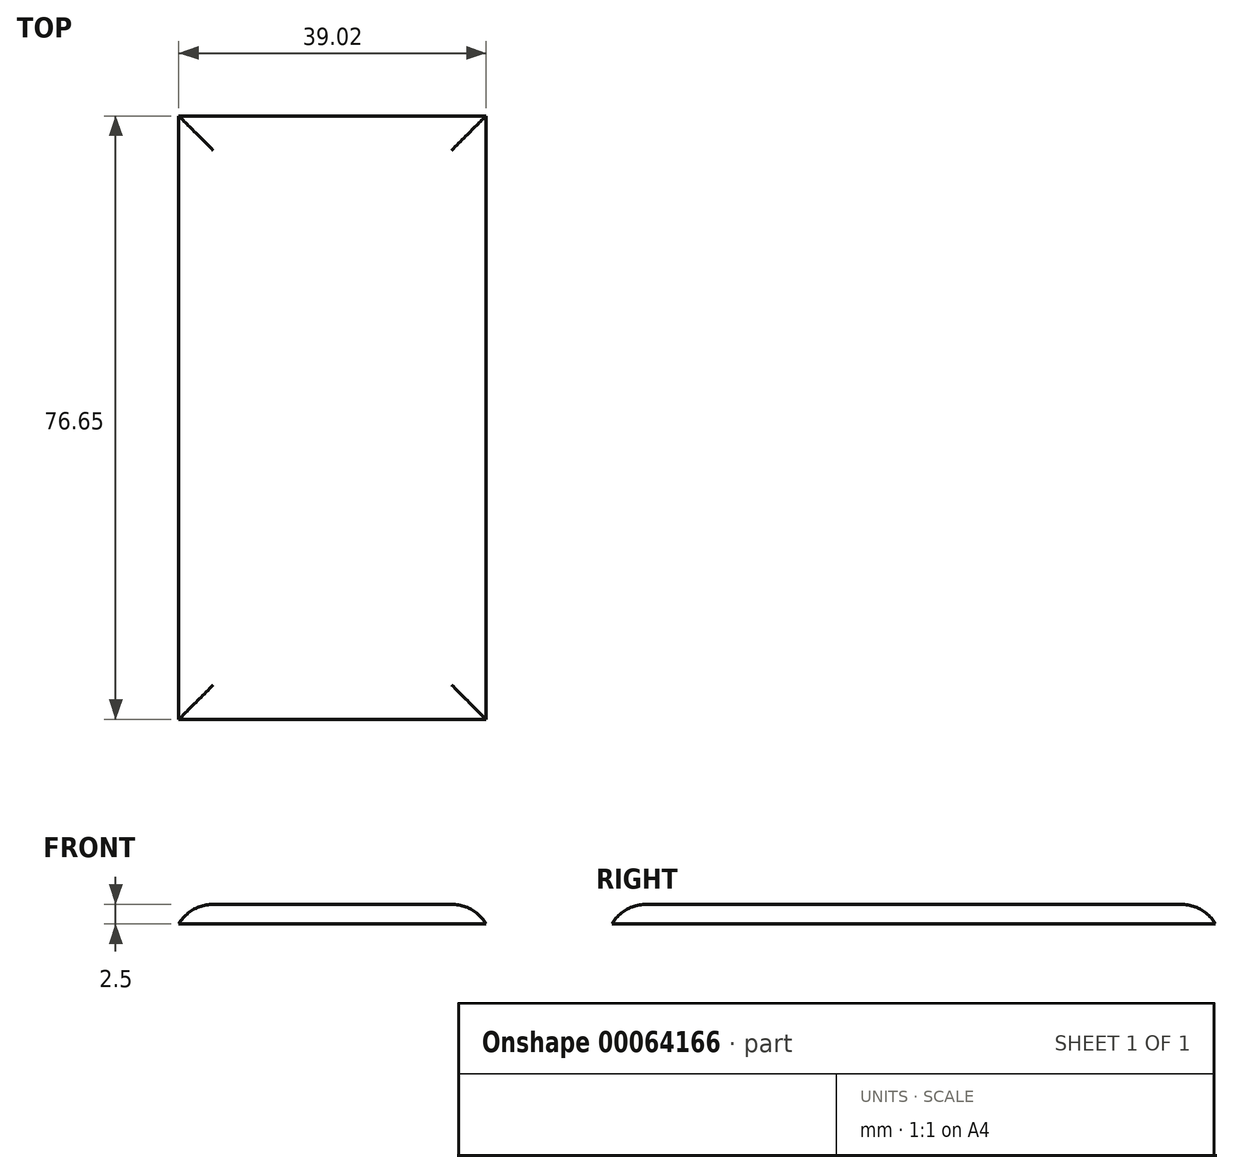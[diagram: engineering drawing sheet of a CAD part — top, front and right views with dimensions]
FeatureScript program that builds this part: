
annotation { "Feature Type Name" : "Feature", "Feature Type Description" : "" }
export const myFeature = defineFeature(function(context is Context, id is Id, definition is map)
    precondition{}
    {
        {
            var Q0;
            Q0=qCreatedBy(makeId("Top.planeOp"),FACE);
            var sketch = newSketch(context, id + "F0", { "sketchPlane" : qUnion([Q0])});
            skLineSegment(sketch, "E0.bottom", {"start": v(-49.75, -34.62) * mm, "end": v(-10.73, -34.62) * mm});
            skLineSegment(sketch, "E0.top", {"start": v(-49.75, 42.03) * mm, "end": v(-10.73, 42.03) * mm});
            skLineSegment(sketch, "E0.left", {"start": v(-49.75, -34.62) * mm, "end": v(-49.75, 42.03) * mm});
            skLineSegment(sketch, "E0.right", {"start": v(-10.73, -34.62) * mm, "end": v(-10.73, 42.03) * mm});
            skSolve(sketch);
        }
        {
            var Q0;
            Q0=makeQuery(id+"F0.imprint","IMPRINT",FACE,{"disambiguationData":[TD([[makeQuery(id+"F0.imprint","IMPRINT",EDGE,{"derivedFrom":sQuery(id+"F0.wireOp",EDGE,"E0.bottom")}),1.0]])]});
            extrude(context, id + "F1", {"entities" : qUnion([Q0]), "depth" : 2.5 * mm});
        }
        {
            var Q0;
            Q0=makeQuery(id+"F1.opExtrude","CAP_EDGE",EDGE,{"disambiguationData":[OSD([sQuery(id+"F0.wireOp",EDGE,"E0.right")])],"isStart":false});
            var Q1;
            Q1=makeQuery(id+"F1.opExtrude","CAP_EDGE",EDGE,{"disambiguationData":[OSD([sQuery(id+"F0.wireOp",EDGE,"E0.bottom")])],"isStart":false});
            var Q2;
            Q2=makeQuery(id+"F1.opExtrude","CAP_EDGE",EDGE,{"disambiguationData":[OSD([sQuery(id+"F0.wireOp",EDGE,"E0.left")])],"isStart":false});
            var Q3;
            Q3=makeQuery(id+"F1.opExtrude","CAP_EDGE",EDGE,{"disambiguationData":[OSD([sQuery(id+"F0.wireOp",EDGE,"E0.top")])],"isStart":false});
            fillet(context, id + "F2", {"entities" : qUnion([Q0, Q1, Q2, Q3]), "radius" : 5.08 * mm, "tangentPropagation" : true, "allowEdgeOverflow" : false});
        }
    });
